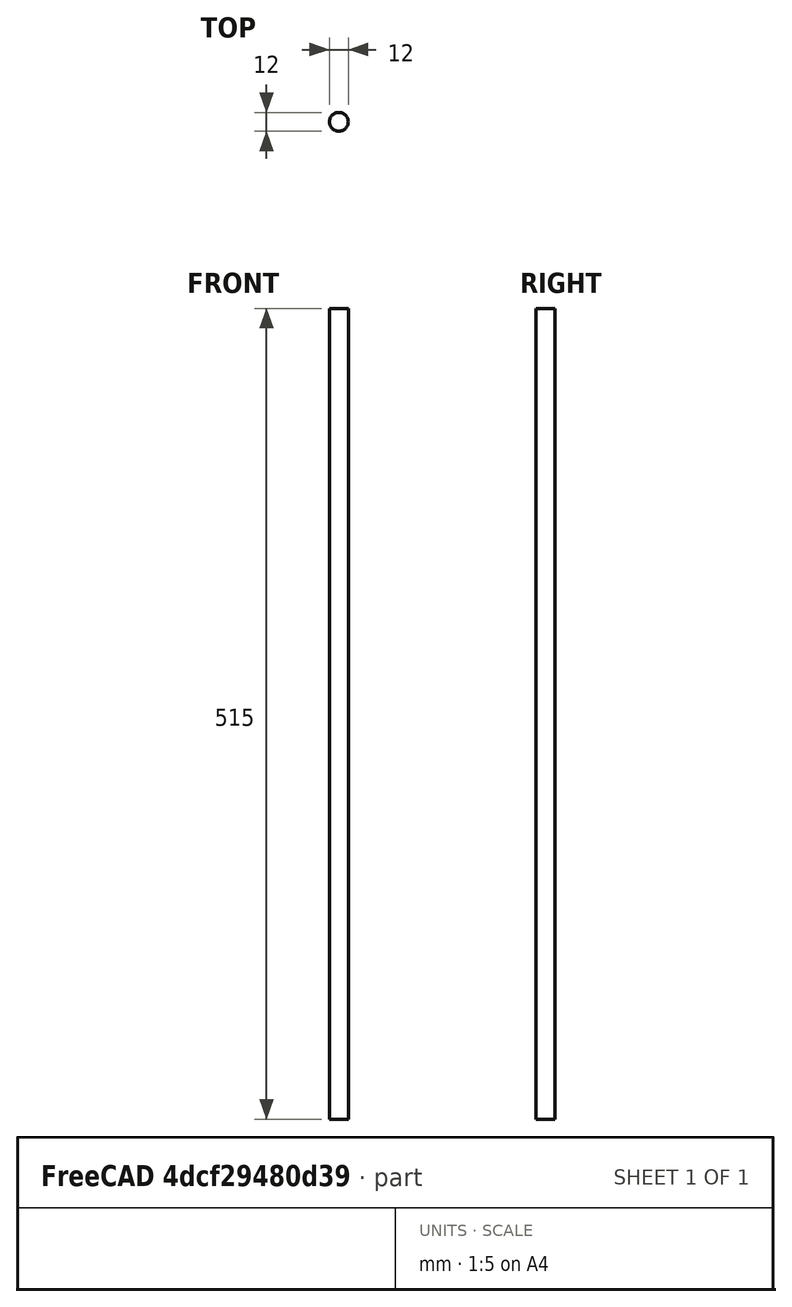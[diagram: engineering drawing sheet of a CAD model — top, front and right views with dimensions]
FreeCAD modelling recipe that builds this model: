
FCSTD DOCUMENT  (FreeCAD 0.16R5480 (Git))
Label: 12mmx515_rod_v1.0
License: All rights reserved
LicenseURL: http://en.wikipedia.org/wiki/All_rights_reserved
objects: Drawing::FeatureViewPython×15, Drawing::FeatureViewPart×2, Sketcher::SketchObject×1, PartDesign::Pad×1, Drawing::FeaturePage×1
note: 3 computed .brp shape members not serialized (recipe doc carries the construction recipe); baked Part::Feature solids carry a one-line shape summary decoded from their .brp

FEATURE [Sketcher::SketchObject] Sketch
  sketch-geometry (1):
    g0: Circle CenterX=0 CenterY=0 CenterZ=0 NormalX=0 NormalY=0 NormalZ=1 Radius=6
  constraints (2):
    c: Coincident(g0,g-1)
    c: Radius(g0) = 6
FEATURE [PartDesign::Pad] Pad
  Length = 515
  Length2 = 100
  Sketch = -> Sketch
  Type = 0
FEATURE [Drawing::FeatureViewPart] Ortho  label="Ortho_0_0"
  Direction = (0,1,0)
  HiddenWidth = 0.15
  LineWidth = 0.35
  Rotation = 0
  Scale = 0.375
  ShowHiddenLines = false
  ShowSmoothLines = false
  Source = -> Pad
  Tolerance = 0.05
  ViewResult = <g id="Ortho_0_0"\n   transform="rotate(0,50,100) translate(50,100) scale(0.375,0.375)"\n  >\n<g   stroke="rgb(0, 0, 0)"\n   stroke-width="0.933333"\n   stroke-linecap="butt"\n   stroke-linejoin="miter"\n   fill="none"\n   transform="scale(1,-1)"\n  >\n<path id= "1" d=" M 515 -6 L 0 -6 " />\n</g>\n<g   stroke="rgb(0, 0, 0)"\n   stroke-width="0.933333"\n   stroke-linecap="butt"\n   stroke-linejoin="miter"\n   fill="none"\n   transform="scale(1,-1)"\n  >\n<path id= "1" d=" M 0 6 L 515 6 " />\n<path d="M0,6 L0,5.84957  L0,5.40581  L0,4.69099  L0,3.74094  L0,2.6033  L0,1.33513  L0,3.67394e-16  L0,-1.33513  L0,-2.6033  L0,-3.74094  L0,-4.69099  L0,-5.40581  L0,-5.84957  L0,-6 " /><path d="M515,6 L515,5.84957  L515,5.40581  L515,4.69099  L515,3.74094  L515,2.6033  L515,1.33513  L515,3.67394e-16  L515,-1.33513  L515,-2.6033  L515,-3.74094  L515,-4.69099  L515,-5.40581  L515,-5.84957  L515,-6 " /></g>\n</g>
  Visible = true
  X = 50
  Y = 100
FEATURE [Drawing::FeatureViewPart] Ortho002  label="Ortho_0_1"
  Direction = (0,0,1)
  HiddenWidth = 0.15
  LineWidth = 0.35
  Rotation = 90
  Scale = 0.38
  ShowHiddenLines = false
  ShowSmoothLines = false
  Source = -> Pad
  Tolerance = 0.05
  ViewResult = <g id="Ortho_0_1"\n   transform="rotate(90,40,100) translate(40,100) scale(0.38,0.38)"\n  >\n<g   stroke="rgb(0, 0, 0)"\n   stroke-width="0.921053"\n   stroke-linecap="butt"\n   stroke-linejoin="miter"\n   fill="none"\n   transform="scale(1,-1)"\n  >\n<circle cx ="0" cy ="0" r ="6" /></g>\n</g>
  Visible = true
  X = 40
  Y = 100
FEATURE [Drawing::FeatureViewPython] dia001  # drawing view (typed FeaturePython)
  Rotation = 0
  ViewResult = <g>  <circle cx ="40.000000" cy ="100.000000" r="0.250000" stroke="none" fill="rgb(0,0,255)" /> \n<line x1="34.755870" y1="88.536006" x2="40.948448" y2="102.073366" style="stroke:rgb(0,0,255);stroke-width:0.50" />\n<polygon points="39.051552,97.926634 38.712965,94.782535 37.387609,94.289150 36.894223,95.614507" style="fill:rgb(0,0,255);stroke:rgb(0,0,255);stroke-width:0" />\n<polygon points="40.948448,102.073366 41.287035,105.217465 42.612391,105.710850 43.105777,104.385493" style="fill:rgb(0,0,255);stroke:rgb(0,0,255);stroke-width:0" />\n<line x1="34.755870" y1="88.536006" x2="15.365753" y2="88.536006" style="stroke:rgb(0,0,255);stroke-width:0.50" />\n<text x="25.060812" y="86.536006" font-family="inherit" font-size="3.6" fill="rgb(0,0,255)" text-anchor="middle" transform="rotate(0.000000 25.060812,86.536006)" >Ø12</text> </g>
  Visible = true
  X = 0
  Y = 0
  arrowL1 = 3
  arrowL2 = 1
  arrowW = 2
  arrow_scheme = 0
  autoPlaceOffset = 2
  autoPlaceText = true
  centerPointDia = 0.5
  click1_x = 34.7559
  click1_y = 88.536
  click2_x = 15.3658
  click2_y = 90.5482
  click3_x = 15.3658
  click3_y = 90.5482
  comma_decimal_place = false
  lineColor = rgb(0,0,255)
  strokeWidth = 0.5
  textFormat_circular = Ø%(value)3.3f
  textRenderer_color = rgb(0,0,255)
  textRenderer_family = inherit
  textRenderer_size = 3.6
  unit_custom_scale = 1
  unit_scheme = 0
FEATURE [Drawing::FeatureViewPython] dim001  # drawing view (typed FeaturePython)
  Rotation = 0
  ViewResult = <g> \n  <line x1="50.000000" y1="95.972821" x2="50.000000" y2="84.975047" style="stroke:rgb(0,0,255);stroke-width:0.50" />\n<line x1="243.125000" y1="95.806411" x2="243.125000" y2="84.975047" style="stroke:rgb(0,0,255);stroke-width:0.50" />\n<line x1="50.000000" y1="85.975047" x2="243.125000" y2="85.975047" style="stroke:rgb(0,0,255);stroke-width:0.50" /> \n  <polygon points="243.125000,85.975047 240.125000,84.975047 239.125000,85.975047 240.125000,86.975047" style="fill:rgb(0,0,255);stroke:rgb(0,0,255);stroke-width:0" /><polygon points="50.000000,85.975047 53.000000,86.975047 54.000000,85.975047 53.000000,84.975047" style="fill:rgb(0,0,255);stroke:rgb(0,0,255);stroke-width:0" /> \n  <text x="146.562500" y="83.975047" font-family="inherit" font-size="3.6" fill="rgb(0,0,255)" text-anchor="middle" transform="rotate(0.000000 146.562500,83.975047)" >515</text> </g>
  Visible = true
  X = 0
  Y = 0
  arrowL1 = 3
  arrowL2 = 1
  arrowW = 2
  arrow_scheme = 0
  autoPlaceOffset = 2
  autoPlaceText = true
  click1_x = 144.969
  click1_y = 85.975
  click2_x = 144.969
  click2_y = 85.975
  comma_decimal_place = false
  dimension_line_overshoot = 1
  gap_datum_points = 2
  halfDimension_linear = false
  lineColor = rgb(0,0,255)
  strokeWidth = 0.5
  textFormat_linear = %(value)3.3f
  textRenderer_color = rgb(0,0,255)
  textRenderer_family = inherit
  textRenderer_size = 3.6
  unit_custom_scale = 1
  unit_scheme = 0
FEATURE [Drawing::FeatureViewPython] tolerance001  # drawing view (typed FeaturePython)
  Rotation = 0
  ViewResult = <g > <text x="38.109507" y="86.536006" font-family="inherit" font-size="2.88" fill="rgb(0,0,255)" text-anchor="end" transform="rotate(0.000000 38.109507,86.536006)" >-0.03</text> \n <text x="38.109507" y="83.656006" font-family="inherit" font-size="2.88" fill="rgb(0,0,255)" text-anchor="end" transform="rotate(0.000000 38.109507,83.656006)" >+0.0</text> </g> 
  Visible = true
  X = 0
  Y = 0
  click1_x = 38.1095
  click1_y = 81.097
  comma_decimal_place = false
  lower_text = -0.03
  toleranceText_sizeRatio = 0.8
  upper_text = +0.0
FEATURE [Drawing::FeatureViewPython] tolerance002  # drawing view (typed FeaturePython)
  Rotation = 0
  ViewResult = <g > <text x="158.535548" y="83.975047" font-family="inherit" font-size="2.88" fill="rgb(0,0,255)" text-anchor="end" transform="rotate(0.000000 158.535548,83.975047)" >-0.0</text> \n <text x="158.535548" y="81.095047" font-family="inherit" font-size="2.88" fill="rgb(0,0,255)" text-anchor="end" transform="rotate(0.000000 158.535548,81.095047)" >+0.05</text> </g> 
  Visible = true
  X = 0
  Y = 0
  click1_x = 158.536
  click1_y = 82.0117
  comma_decimal_place = false
  lower_text = 0
  toleranceText_sizeRatio = 0.8
  upper_text = +0.05
FEATURE [Drawing::FeatureViewPython] centerLines001  # drawing view (typed FeaturePython)
  Rotation = 0
  ViewResult = <g transform="scale(0.380000,0.380000)" stroke="rgb(0,0,255)"  stroke-width="0.842105" > <path d="M 105.263158,263.157895 L 105.263158,255.263158 M 105.263158,250.000000 L 105.263158,248.714675 "/>\n<path d="M 105.263158,263.157895 L 113.157895,263.157895 M 118.421053,263.157895 L 120.345810,263.157895 "/>\n<path d="M 105.263158,263.157895 L 105.263158,271.052632 M 105.263158,276.315789 L 105.263158,278.399975 "/>\n<path d="M 105.263158,263.157895 L 97.368421,263.157895 M 92.105263,263.157895 L 87.852442,263.157895 "/> </g> 
  Visible = true
  X = 0
  Y = 0
  centerLine_color = rgb(0,0,255)
  centerLine_len_dash = 6
  centerLine_len_dot = 3
  centerLine_len_gap = 2
  centerLine_width = 0.32
  click1_x = 45.7314
  click1_y = 94.5116
  click2_x = 33.3839
  click2_y = 105.792
FEATURE [Drawing::FeatureViewPython] centerLines002  # drawing view (typed FeaturePython)
  Rotation = 0
  ViewResult = <g transform="scale(0.375000,0.375000)" stroke="rgb(0,0,255)"  stroke-width="0.853333" > <path d="M 390.833333,266.666667 L 382.833333,266.666667 M 377.500000,266.666667 L 361.500000,266.666667 M 356.166667,266.666667 L 348.166667,266.666667 M 342.833333,266.666667 L 326.833333,266.666667 M 321.500000,266.666667 L 313.500000,266.666667 M 308.166667,266.666667 L 292.166667,266.666667 M 286.833333,266.666667 L 278.833333,266.666667 M 273.500000,266.666667 L 257.500000,266.666667 M 252.166667,266.666667 L 244.166667,266.666667 M 238.833333,266.666667 L 222.833333,266.666667 M 217.500000,266.666667 L 209.500000,266.666667 M 204.166667,266.666667 L 188.166667,266.666667 M 182.833333,266.666667 L 174.833333,266.666667 M 169.500000,266.666667 L 153.500000,266.666667 M 148.166667,266.666667 L 140.166667,266.666667 M 134.833333,266.666667 L 128.207908,266.666667 "/>\n<path d="M 390.833333,266.666667 L 398.833333,266.666667 M 404.166667,266.666667 L 420.166667,266.666667 M 425.500000,266.666667 L 433.500000,266.666667 M 438.833333,266.666667 L 454.833333,266.666667 M 460.166667,266.666667 L 468.166667,266.666667 M 473.500000,266.666667 L 489.500000,266.666667 M 494.833333,266.666667 L 502.833333,266.666667 M 508.166667,266.666667 L 524.166667,266.666667 M 529.500000,266.666667 L 537.500000,266.666667 M 542.833333,266.666667 L 558.833333,266.666667 M 564.166667,266.666667 L 572.166667,266.666667 M 577.500000,266.666667 L 593.500000,266.666667 M 598.833333,266.666667 L 606.833333,266.666667 M 612.166667,266.666667 L 628.166667,266.666667 M 633.500000,266.666667 L 641.500000,266.666667 M 646.833333,266.666667 L 659.388562,266.666667 "/> </g> 
  Visible = true
  X = 0
  Y = 0
  centerLine_color = rgb(0,0,255)
  centerLine_len_dash = 6
  centerLine_len_dot = 3
  centerLine_len_gap = 2
  centerLine_width = 0.32
  click1_x = 48.078
  click1_y = 100.567
  click2_x = 247.271
  click2_y = 99.4199
FEATURE [Drawing::FeatureViewPython] text005  # drawing view (typed FeaturePython)
  Rotation = 0
  ViewResult = <g> <text x="25.883061" y="9.184312" font-family="inherit" font-size="3" fill="rgb(0,0,0)" text-anchor="inherit" transform="rotate(0.000000 25.883061,9.184312)" >6</text> </g>
  Visible = true
  X = 0
  Y = 0
  click1_x = 25.8831
  click1_y = 9.18431
  rotation = 0
  text = 6
  textRenderer_addText_color = rgb(0,0,0)
  textRenderer_addText_family = inherit
  textRenderer_addText_size = 3
FEATURE [Drawing::FeatureViewPython] weld001  # drawing view (typed FeaturePython)
  Rotation = 0
  ViewResult = <g   >\n<line x1="156.396477" y1="117.441635" x2="146.562500" y2="102.250000" style="stroke:rgb(0,0,255);stroke-width:0.50" />\n<polygon points="146.562500,102.250000 147.353265,105.311812 148.736143,105.607868 149.032199,104.224990" style="fill:rgb(0,0,255);stroke:rgb(0,0,255);stroke-width:0" />\n<line x1="156.396477" y1="117.441635" x2="233.151943" y2="117.441635" style="stroke:rgb(0,0,255);stroke-width:0.50" />\n</g> 
  Visible = true
  X = 0
  Y = 0
  arrowL1 = 3
  arrowL2 = 1
  arrowW = 2
  click1_x = 156.396
  click1_y = 117.442
  click2_x = 233.152
  click2_y = 127.541
  lineColor = rgb(0,0,255)
  strokeWidth = 0.5
  textRenderer_color = rgb(0,0,255)
  textRenderer_family = inherit
  textRenderer_size = 3.6
FEATURE [Drawing::FeatureViewPython] text006  # drawing view (typed FeaturePython)
  Rotation = 0
  ViewResult = <g> <text x="158.704912" y="115.421754" font-family="inherit" font-size="5" fill="rgb(0,0,0)" text-anchor="inherit" transform="rotate(0.000000 158.704912,115.421754)" >Straightness 0.1mm per 100mm</text> </g>
  Visible = true
  X = 0
  Y = 0
  click1_x = 158.705
  click1_y = 115.422
  rotation = 0
  text = Straightness 0.1mm per 100mm
  textRenderer_addText_color = rgb(0,0,0)
  textRenderer_addText_family = inherit
  textRenderer_addText_size = 5
FEATURE [Drawing::FeatureViewPython] text007  # drawing view (typed FeaturePython)
  Rotation = 0
  ViewResult = <g> <text x="20.083385" y="119.115250" font-family="inherit" font-size="5" fill="rgb(0,0,0)" text-anchor="inherit" transform="rotate(0.000000 20.083385,119.115250)" >NOTES:</text> </g>
  Visible = true
  X = 0
  Y = 0
  click1_x = 20.0834
  click1_y = 119.115
  rotation = 0
  text = NOTES:
  textRenderer_addText_color = rgb(0,0,0)
  textRenderer_addText_family = inherit
  textRenderer_addText_size = 5
FEATURE [Drawing::FeatureViewPython] text008  # drawing view (typed FeaturePython)
  Rotation = 0
  ViewResult = <g> <text x="19.390855" y="127.425616" font-family="inherit" font-size="5" fill="rgb(0,0,0)" text-anchor="inherit" transform="rotate(0.000000 19.390855,127.425616)" >1.  Parts must be free of all burrs and sharp edges.</text> </g>
  Visible = true
  X = 0
  Y = 0
  click1_x = 19.3909
  click1_y = 127.426
  rotation = 0
  text = 1.  Parts must be free of all burrs and sharp edges.
  textRenderer_addText_color = rgb(0,0,0)
  textRenderer_addText_family = inherit
  textRenderer_addText_size = 5
FEATURE [Drawing::FeatureViewPython] text001  # drawing view (typed FeaturePython)
  Rotation = 0
  ViewResult = <g> <text x="19.477421" y="135.139637" font-family="inherit" font-size="5" fill="rgb(0,0,0)" text-anchor="inherit" transform="rotate(0.000000 19.477421,135.139637)" >2.  Rods must be consistently smooth and not contain pits or gouges.</text> </g>
  Visible = true
  X = 0
  Y = 0
  click1_x = 19.4774
  click1_y = 135.14
  rotation = 0
  text = 2.  Rods must be consistently smooth and not contain pits or gouges.
  textRenderer_addText_color = rgb(0,0,0)
  textRenderer_addText_family = inherit
  textRenderer_addText_size = 5
FEATURE [Drawing::FeatureViewPython] text002  # drawing view (typed FeaturePython)
  Rotation = 0
  ViewResult = <g> <text x="19.236959" y="142.113035" font-family="inherit" font-size="5" fill="rgb(0,0,0)" text-anchor="inherit" transform="rotate(0.000000 19.236959,142.113035)" >3.  Surface finish Ra 0.3</text> </g>
  Visible = true
  X = 0
  Y = 0
  click1_x = 19.237
  click1_y = 142.113
  rotation = 0
  text = 3.  Surface finish Ra 0.3
  textRenderer_addText_color = rgb(0,0,0)
  textRenderer_addText_family = inherit
  textRenderer_addText_size = 5
FEATURE [Drawing::FeatureViewPython] text003  # drawing view (typed FeaturePython)
  Rotation = 0
  ViewResult = <g> <text x="18.996497" y="149.326894" font-family="inherit" font-size="5" fill="rgb(0,0,0)" text-anchor="inherit" transform="rotate(0.000000 18.996497,149.326894)" >4.  All parts must be RoHS compliant</text> </g>
  Visible = true
  X = 0
  Y = 0
  click1_x = 18.9965
  click1_y = 149.327
  rotation = 0
  text = 4.  All parts must be RoHS compliant
  textRenderer_addText_color = rgb(0,0,0)
  textRenderer_addText_family = inherit
  textRenderer_addText_size = 5
FEATURE [Drawing::FeatureViewPython] text004  # drawing view (typed FeaturePython)
  Rotation = 0
  ViewResult = <g> <text x="19.236959" y="156.781216" font-family="inherit" font-size="5" fill="rgb(0,0,0)" text-anchor="inherit" transform="rotate(0.000000 19.236959,156.781216)" >5.  Material: 304 Stainless Steel</text> </g>
  Visible = true
  X = 0
  Y = 0
  click1_x = 19.237
  click1_y = 156.781
  rotation = 0
  text = 5.  Material: 304 Stainless Steel
  textRenderer_addText_color = rgb(0,0,0)
  textRenderer_addText_family = inherit
  textRenderer_addText_size = 5
FEATURE [Drawing::FeaturePage] Page
  EditableTexts = J PETTIT | 04.25.16 | Scale | 12mm Smooth Rod, SS, 515mm | IR | HD-RD0047 | 1 of 1 | 304 Stainless
  Group = -> [Ortho,Ortho002,dia001,dim001,tolerance001,tolerance002,centerLines001,centerLines002,text005,weld001,text006,text007,text008,text001,text002,text003,text004]
